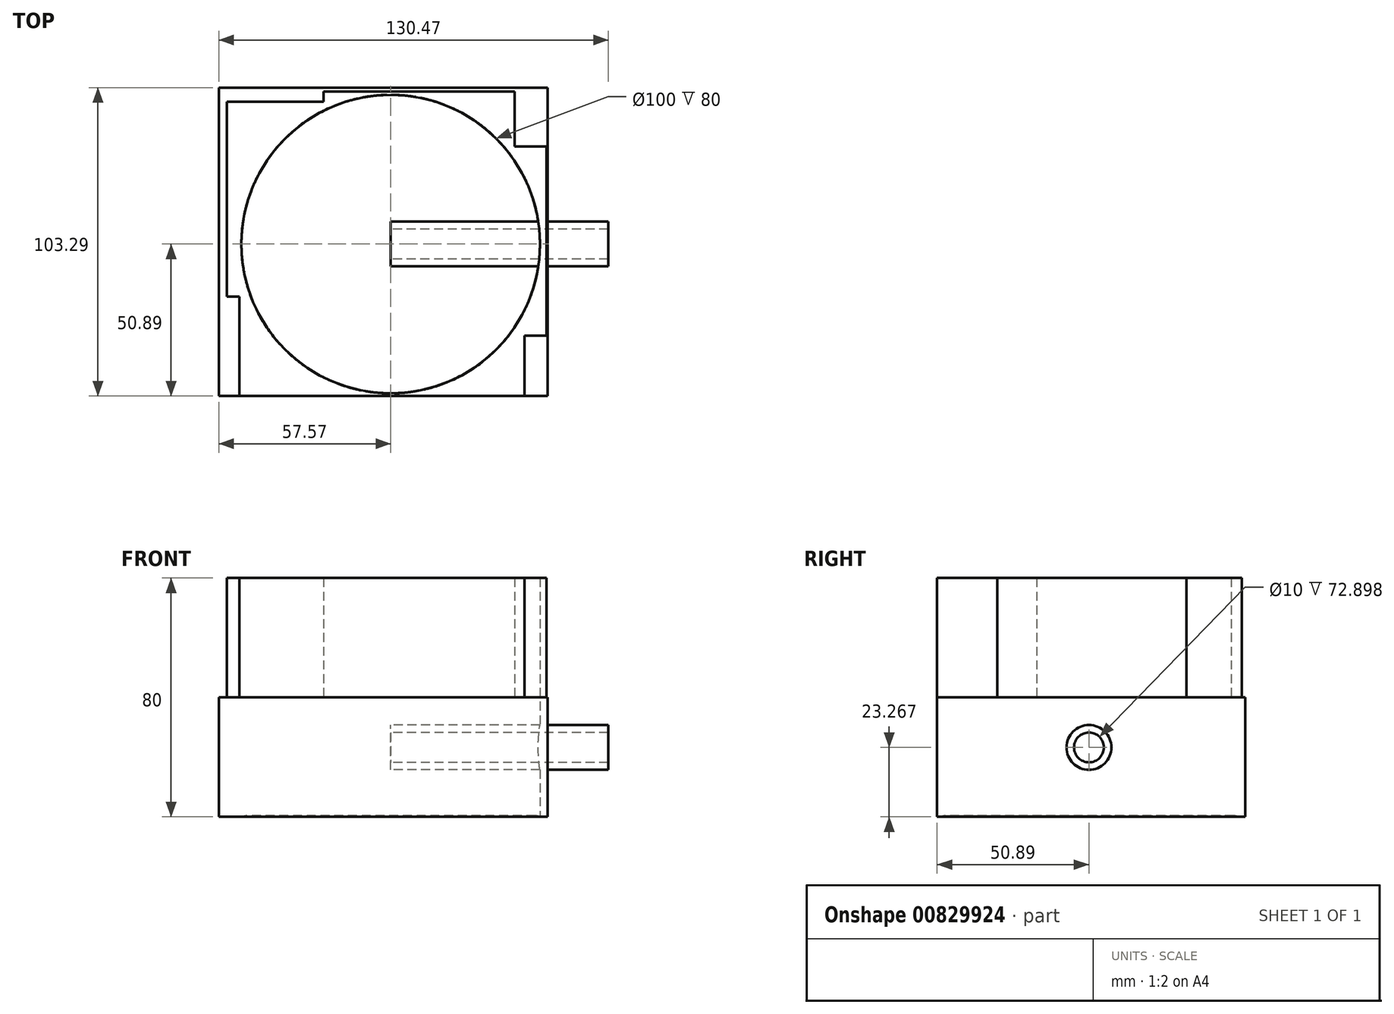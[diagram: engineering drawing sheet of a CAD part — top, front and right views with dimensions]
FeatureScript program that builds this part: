
annotation { "Feature Type Name" : "Feature", "Feature Type Description" : "" }
export const myFeature = defineFeature(function(context is Context, id is Id, definition is map)
    precondition{}
    {
        {
            var Q0;
            Q0=qCreatedBy(makeId("Top.planeOp"),FACE);
            var sketch = newSketch(context, id + "F0", { "sketchPlane" : qUnion([Q0])});
            skCircle(sketch, "E0", {"center": v(0, 0) * mm, "radius": 50 * mm});
            skLineSegment(sketch, "E1.bottom", {"start": v(-57.57, 52.4) * mm, "end": v(52.62, 52.4) * mm});
            skLineSegment(sketch, "E1.top", {"start": v(-57.57, -50.9) * mm, "end": v(52.62, -50.9) * mm});
            skLineSegment(sketch, "E1.left", {"start": v(-57.57, 52.4) * mm, "end": v(-57.57, -50.9) * mm});
            skLineSegment(sketch, "E1.right", {"start": v(52.62, 52.4) * mm, "end": v(52.62, -50.9) * mm});
            skSolve(sketch);
        }
        {
            var Q0;
            Q0=makeQuery(id+"F0.imprint","IMPRINT",FACE,{"disambiguationData":[TD([[makeQuery(id+"F0.imprint","IMPRINT",EDGE,{"derivedFrom":sQuery(id+"F0.wireOp",EDGE,"E0")}),1.0]])]});
            extrude(context, id + "F1", {"entities" : qUnion([Q0]), "depth" : .4 * mm, "offsetDistance" : 25.4 * mm});
        }
        {
            var Q0;
            Q0=makeQuery(id+"F1.opExtrude","CAP_EDGE",EDGE,{"disambiguationData":[OSD([sQuery(id+"F0.wireOp",EDGE,"E0")])],"isStart":false});
            fillet(context, id + "F2", {"entities" : qUnion([Q0]), "radius" : 3 * mm, "tangentPropagation" : true, "rho" : .5, "crossSection" : FilletCrossSection.CONIC, "allowEdgeOverflow" : false});
        }
        {
            var Q0;
            Q0=makeQuery(id+"F0.imprint","IMPRINT",FACE,{"disambiguationData":[TD([[makeQuery(id+"F0.imprint","IMPRINT",EDGE,{"derivedFrom":sQuery(id+"F0.wireOp",EDGE,"E0")}),-1.0]])]});
            extrude(context, id + "F3", {"entities" : qUnion([Q0]), "operationType" : NewBodyOperationType.ADD, "depth" : 40 * mm, "offsetDistance" : 25.4 * mm});
        }
        {
            var Q0;
            Q0=qCreatedBy(makeId("Top.planeOp"),FACE);
            var sketch = newSketch(context, id + "F4", { "sketchPlane" : qUnion([Q0])});
            skCircle(sketch, "E2", {"center": v(0, 0) * mm, "radius": 50 * mm});
            skLineSegment(sketch, "E3.bottom", {"start": v(-54.86, 47.62) * mm, "end": v(0, 47.62) * mm});
            skLineSegment(sketch, "E3.top", {"start": v(-54.86, -17.56) * mm, "end": v(0, -17.56) * mm});
            skLineSegment(sketch, "E3.left", {"start": v(-54.86, 47.62) * mm, "end": v(-54.86, -17.56) * mm});
            skLineSegment(sketch, "E3.right", {"start": v(0, 47.62) * mm, "end": v(0, -17.56) * mm});
            skLineSegment(sketch, "E4.bottom", {"start": v(-22.5, 51.15) * mm, "end": v(41.47, 51.15) * mm});
            skLineSegment(sketch, "E4.top", {"start": v(-22.5, -10.75) * mm, "end": v(41.47, -10.75) * mm});
            skLineSegment(sketch, "E4.left", {"start": v(-22.5, 51.15) * mm, "end": v(-22.5, -10.75) * mm});
            skLineSegment(sketch, "E4.right", {"start": v(41.47, 51.15) * mm, "end": v(41.47, -10.75) * mm});
            skLineSegment(sketch, "E5.bottom", {"start": v(52.23, 32.7) * mm, "end": v(-13.17, 32.7) * mm});
            skLineSegment(sketch, "E5.top", {"start": v(52.23, -30.72) * mm, "end": v(-13.17, -30.72) * mm});
            skLineSegment(sketch, "E5.left", {"start": v(52.23, 32.7) * mm, "end": v(52.23, -30.72) * mm});
            skLineSegment(sketch, "E5.right", {"start": v(-13.17, 32.7) * mm, "end": v(-13.17, -30.72) * mm});
            skLineSegment(sketch, "E6.bottom", {"start": v(-50.7, -50.87) * mm, "end": v(44.87, -50.87) * mm});
            skLineSegment(sketch, "E6.top", {"start": v(-50.7, -17.56) * mm, "end": v(44.87, -17.56) * mm});
            skLineSegment(sketch, "E6.left", {"start": v(-50.7, -50.87) * mm, "end": v(-50.7, -17.56) * mm});
            skLineSegment(sketch, "E6.right", {"start": v(44.87, -50.87) * mm, "end": v(44.87, -17.56) * mm});
            skSolve(sketch);
        }
        {
            var Q0;
            Q0 = qSketchRegion(id + "F4", true);
            extrude(context, id + "F5", {"entities" : qUnion([Q0]), "operationType" : NewBodyOperationType.ADD, "depth" : 80 * mm, "offsetDistance" : 25.4 * mm, "hasSecondDirection" : true, "secondDirectionOppositeDirection" : true, "secondDirectionDepth" : -40 * mm});
        }
        {
            var Q0;
            Q0=qCreatedBy(makeId("Right.planeOp"),FACE);
            var sketch = newSketch(context, id + "F6", { "sketchPlane" : qUnion([Q0])});
            skPoint(sketch, "E7", {"position": v(0, 23.27) * mm});
            skSolve(sketch);
        }
        {
            var Q0;
            Q0=sQuery(id+"F6.wireOp",VERTEX,"E7");
            var Q1;
            Q1=makeQuery(id+"F3.opExtrude","SWEPT_BODY",BODY,{"disambiguationData":[OSD([sQuery(id+"F0.wireOp",EDGE,"E0"),sQuery(id+"F0.wireOp",EDGE,"E1.bottom"),sQuery(id+"F0.wireOp",EDGE,"E1.top"),sQuery(id+"F0.wireOp",EDGE,"E1.left"),sQuery(id+"F0.wireOp",EDGE,"E1.right")])]});
            hole(context, id + "F7", {"style" : HoleStyle.SIMPLE, "endStyle" : HoleEndStyle.THROUGH, "oppositeDirection" : true, "holeDiameter" : 15 * mm, "majorDiameter" : 6.35 * mm, "isTappedThrough" : true, "tappedDepth" : 12.7 * mm, "tapClearance" : 3, "locations" : qUnion([Q0]), "scope" : qUnion([Q1])});
        }
        {
            var Q0;
            Q0=qCreatedBy(makeId("Right.planeOp"),FACE);
            var sketch = newSketch(context, id + "F8", { "sketchPlane" : qUnion([Q0])});
            skCircle(sketch, "E8", {"center": v(0, 23.27) * mm, "radius": 7.5 * mm});
            skSolve(sketch);
        }
        {
            var Q0;
            Q0=makeQuery(id+"F8.imprint","IMPRINT",FACE,{"disambiguationData":[TD([[makeQuery(id+"F8.imprint","IMPRINT",EDGE,{"derivedFrom":sQuery(id+"F8.wireOp",EDGE,"E8")}),1.0]])]});
            extrude(context, id + "F9", {"entities" : qUnion([Q0]), "operationType" : NewBodyOperationType.ADD, "depth" : 72.9 * mm, "offsetDistance" : 25.4 * mm});
        }
        {
            var Q0;
            Q0=sQuery(id+"F8.wireOp",VERTEX,"E8.center");
            var Q1;
            Q1=makeQuery(id+"F3.opExtrude","SWEPT_BODY",BODY,{"disambiguationData":[OSD([sQuery(id+"F0.wireOp",EDGE,"E0"),sQuery(id+"F0.wireOp",EDGE,"E1.bottom"),sQuery(id+"F0.wireOp",EDGE,"E1.top"),sQuery(id+"F0.wireOp",EDGE,"E1.left"),sQuery(id+"F0.wireOp",EDGE,"E1.right")])]});
            hole(context, id + "F10", {"style" : HoleStyle.SIMPLE, "endStyle" : HoleEndStyle.THROUGH, "oppositeDirection" : true, "holeDiameter" : 10 * mm, "majorDiameter" : 6.35 * mm, "isTappedThrough" : true, "tappedDepth" : 12.7 * mm, "tapClearance" : 3, "locations" : qUnion([Q0]), "scope" : qUnion([Q1])});
        }
    });
